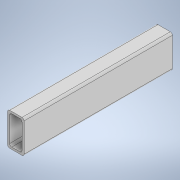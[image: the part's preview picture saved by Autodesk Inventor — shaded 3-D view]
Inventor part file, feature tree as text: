
AUTODESK INVENTOR PART (.ipt)
format: ipt  version: 2020 (Build 240168000, 168)  size: 122,368 bytes
history: native  units: in
note: dims shown in document units (in); Inventor stores cm internally (conversion verified against a paired STEP export)
features: extrude x1, sketch x1
ambient origin geometry x8: Origin, YZ Plane, XZ Plane, XY Plane, X Axis, Y Axis, Z Axis, Center Point
bodies: Solid1 (feature_tree)
feature tree (2):
  extrude  "Extrusion1"  Depth=1.0in
  sketch  "Sketch1"  dims[d0=2.0in d1=1.0in d2=0.125in d3=0.125in d4=0.125in d5=0.125in d6=0.125in d7=0.125in d8=0.125in d9=0.125in d10=0.125in d11=9.0in d12=0.0in]
